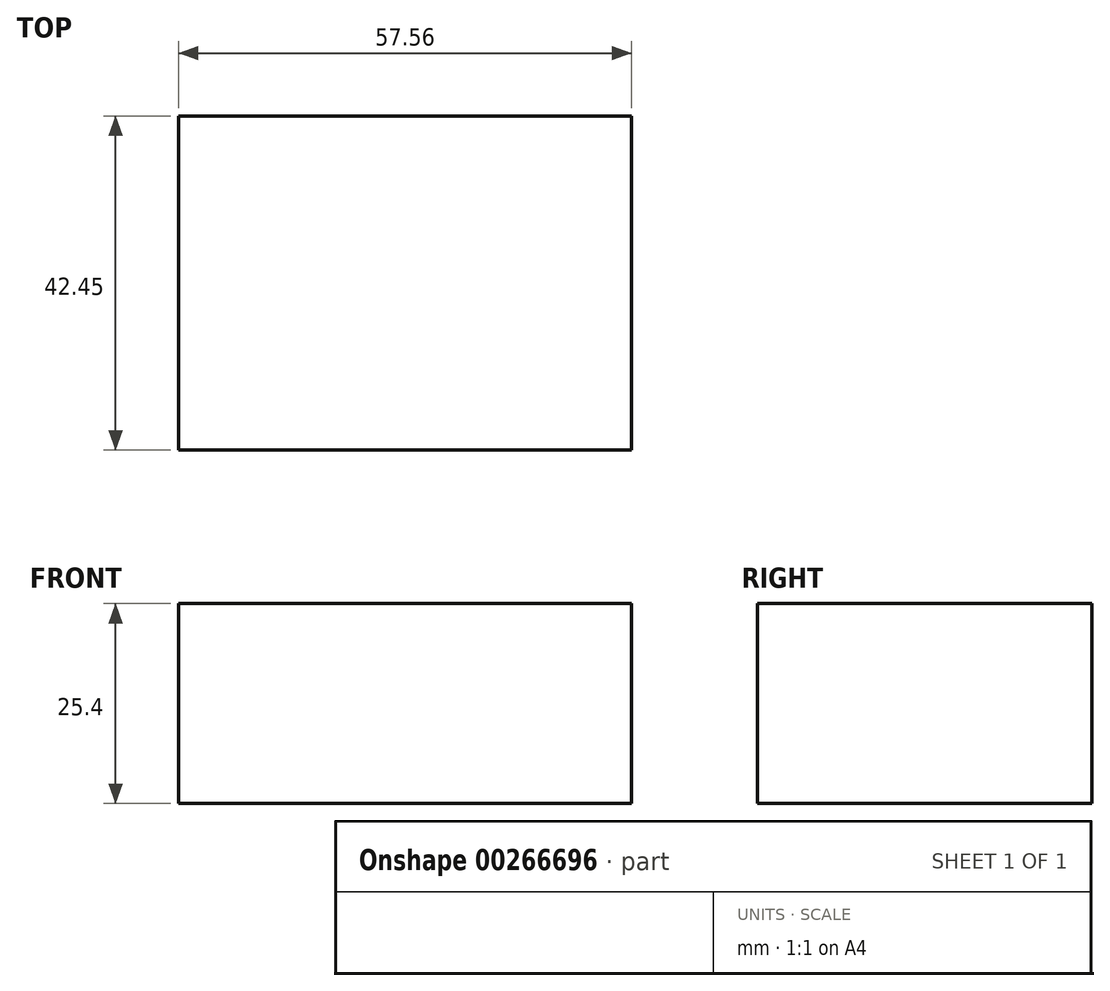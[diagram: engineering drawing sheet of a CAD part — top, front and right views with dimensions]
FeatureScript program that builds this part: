
annotation { "Feature Type Name" : "Feature", "Feature Type Description" : "" }
export const myFeature = defineFeature(function(context is Context, id is Id, definition is map)
    precondition{}
    {
        {
            var Q0;
            Q0=qCreatedBy(makeId("Top.planeOp"),FACE);
            var sketch = newSketch(context, id + "F0", { "sketchPlane" : qUnion([Q0])});
            skLineSegment(sketch, "E0.bottom", {"start": v(-38.4, 23.13) * mm, "end": v(19.15, 23.13) * mm});
            skLineSegment(sketch, "E0.top", {"start": v(-38.4, -19.32) * mm, "end": v(19.15, -19.32) * mm});
            skLineSegment(sketch, "E0.left", {"start": v(-38.4, 23.13) * mm, "end": v(-38.4, -19.32) * mm});
            skLineSegment(sketch, "E0.right", {"start": v(19.15, 23.13) * mm, "end": v(19.15, -19.32) * mm});
            skSolve(sketch);
        }
        {
            var Q0;
            Q0 = qSketchRegion(id + "F0", true);
            extrude(context, id + "F1", {"entities" : qUnion([Q0]), "depth" : 25.4 * mm});
        }
    });
